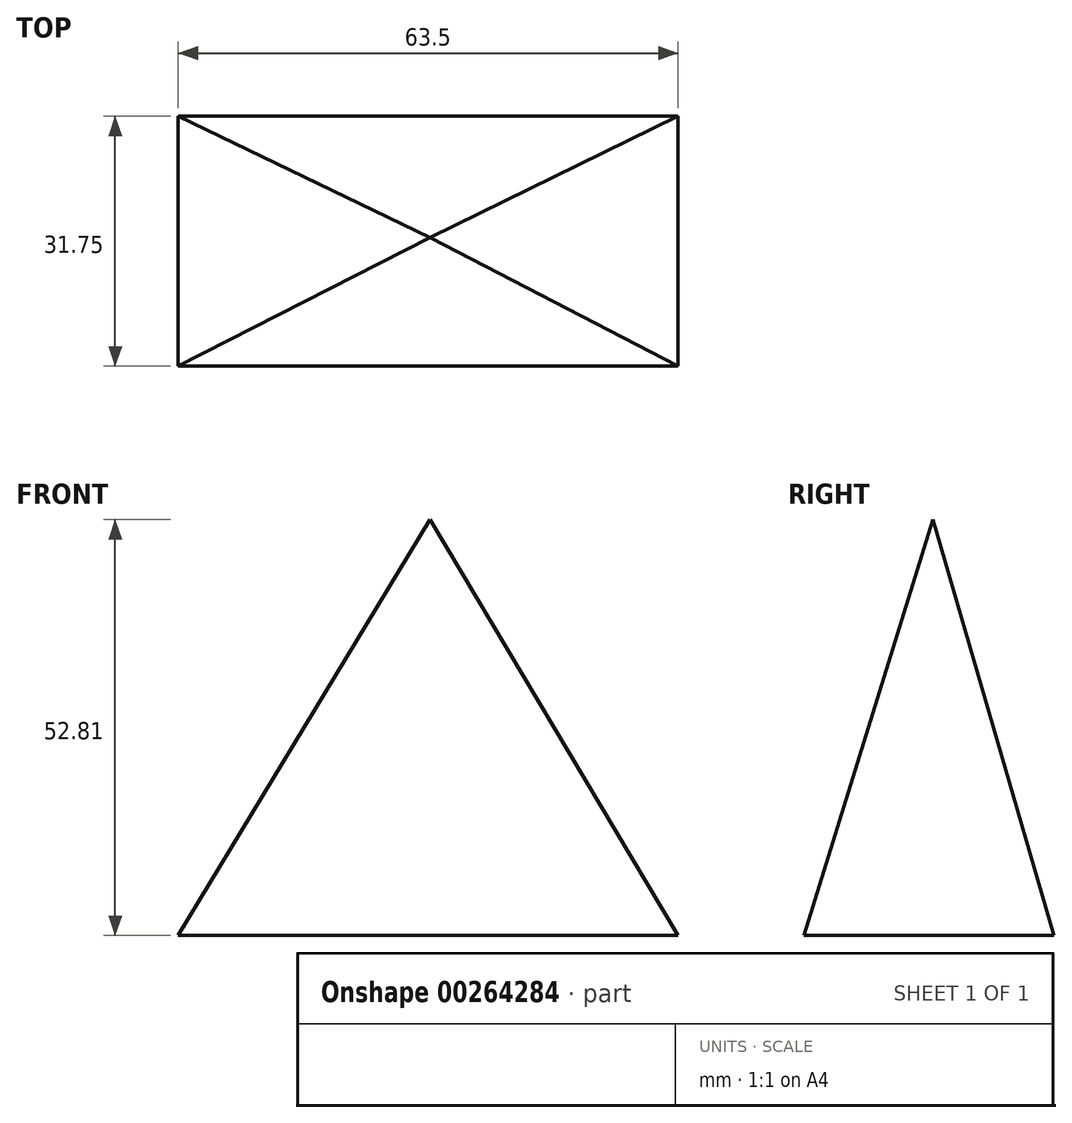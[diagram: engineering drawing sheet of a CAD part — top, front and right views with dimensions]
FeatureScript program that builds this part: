
annotation { "Feature Type Name" : "Feature", "Feature Type Description" : "" }
export const myFeature = defineFeature(function(context is Context, id is Id, definition is map)
    precondition{}
    {
        {
            var Q0;
            Q0=qCreatedBy(makeId("Top.planeOp"),FACE);
            var sketch = newSketch(context, id + "F0", { "sketchPlane" : qUnion([Q0])});
            skLineSegment(sketch, "E0.bottom", {"start": v(-31.98, -16.34) * mm, "end": v(31.52, -16.34) * mm});
            skLineSegment(sketch, "E0.top", {"start": v(-31.98, 15.41) * mm, "end": v(31.52, 15.41) * mm});
            skLineSegment(sketch, "E0.left", {"start": v(-31.98, -16.34) * mm, "end": v(-31.98, 15.41) * mm});
            skLineSegment(sketch, "E0.right", {"start": v(31.52, -16.34) * mm, "end": v(31.52, 15.41) * mm});
            skPoint(sketch, "E1", {"position": v(0, -16.34) * mm});
            skSolve(sketch);
        }
        {
            var Q0;
            Q0=qCreatedBy(makeId("Front.planeOp"),FACE);
            var sketch = newSketch(context, id + "F1", { "sketchPlane" : qUnion([Q0])});
            skPoint(sketch, "E2", {"position": v(0, 52.8) * mm});
            skSolve(sketch);
        }
        {
            var Q0;
            Q0=makeQuery(id+"F0.imprint","IMPRINT",FACE,{"disambiguationData":[TD([[makeQuery(id+"F0.imprint","IMPRINT",EDGE,{"derivedFrom":sQuery(id+"F0.wireOp",EDGE,"E0.bottom")}),1.0]])]});
            var Q1;
            Q1=sQuery(id+"F1.wireOp",VERTEX,"E2");
            loft(context, id + "F2", {"sheetProfilesArray" : [{ "sheetProfileEntities" : qUnion([Q0]) }, { "sheetProfileEntities" : qUnion([Q1]) }]});
        }
    });
